# Revit family: Sanitary_Taps&Mixers_Zurn__Z824B0-XL
name_source: partatom
category: Plumbing Fixtures
units: mm (PartAtom-declared; Revit-internal decimal feet)

## family parameters
Cut with Voids When Loaded = No
Host = Face
Maintain Annotation Orientation = No
OmniClass Number = 23.45.55.17
OmniClass Title = Mixing Faucets
Part Type = Normal
Room Calculation Point = No
Round Connector Dimension = Use Radius
Shared = No

## types (10) — shared parameters
ADA Compliance = Yes
Assembly Code = D2010
CW Connection = Yes
CWFU = 1
Default Elevation = 34"
Description = Single Control Faucet
Distance Between Spout to Handle centers = 4"
HW Connection = Yes
HWFU = 1
Height from Spout Base to Aerator = 6 1/2"
Inlet Connection Size (inch) = 1/2"
Lead-Free Compliant = Yes
Manufacturer = Zurn Water, LLC
Manufacturer Brand = Zurn
Model = Z824B0-XL
Modified Date = 09/12/2025
Product Documentation Link = https://files.zurn.com
Product Page URL = https://www.zurn.com
Product data URL = https://bimobject.com
Spout Height from Base = 11"
Spout Length = 5 1/2"
URL = www.zurn.com
Vent Connection = No
Waste Connection = No
Water Sense Compliance = No
Width of Handle = 4"
zero-valued in all types: WFU

## per-type parameters (varying)
| type | Flow Rate | Main Material | Types of Outlet |
| Z824B0-XL-2F (2.2 GPM AERATOR OUTLET) | 1 GPM | Chrome-Plated Brass - Zurn - Polished | SPRAY |
| Z824B0-XL-3F (0.5 GPM SPRAY OUTLET) | 1 GPM | Metal - Zurn - Polished Chrome-Finish | SPRAY |
| Z824B0-XL-4F (2.2 GPM LAMINAR OUTLET) | 2 GPM | Metal - Zurn - Polished Chrome-Finish | LAMINAR |
| Z824B0-XL-7F (1.0 GPM SPRAY OUTLET) | 1 GPM | Chrome-Plated Brass - Zurn - Polished | SPRAY |
| Z824B0-XL-16F (1.0 GPM SPRAY OUTLET) | 1 GPM | Metal - Zurn - Polished Chrome-Finish | SPRAY |
| Z824B0-XL-17F (1.5 GPM AERATOR OUTLET) | 2 GPM | Metal - Zurn - Polished Chrome-Finish | AERATOR |
| Z824B0-XL-18F (1.5 GPM LAMINAR OUTLET) | 2 GPM | Metal - Zurn - Polished Chrome-Finish | LAMINAR |
| Z824B0-XL-22F (1.0 GPM LAMINAR OUTLET) | 1 GPM | Metal - Zurn - Polished Chrome-Finish | LAMINAR |
| Z824B0-XL-25F (0.35 GPM SPRAY OUTLET) | 0 GPM | Metal - Zurn - Polished Chrome-Finish | SPRAY |
| Z824B0-XL-28F (0.5 GPM LAMINAR OUTLET) | 1 GPM | Metal - Zurn - Polished Chrome-Finish | LAMINAR |

## geometry (parser evidence)
native form markers: Sweep x2
no freeform markers — native parametric forms only
